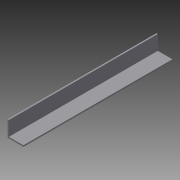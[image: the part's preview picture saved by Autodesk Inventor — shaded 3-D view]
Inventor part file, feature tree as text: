
AUTODESK INVENTOR PART (.ipt)
format: ipt  version: 2015 (Build 190159000, 159)  size: 77,824 bytes
history: native  units: in
note: dims shown in document units (in); Inventor stores cm internally (conversion verified against a paired STEP export)
features: extrude x2, sketch x2
ambient origin geometry x8: Origin, YZ Plane, XZ Plane, XY Plane, X Axis, Y Axis, Z Axis, Center Point
bodies: Solid1 (feature_tree)
feature tree (4):
  extrude  "Extrusion1"  Depth=0.125in
  extrude  "Extrusion2"  Depth=0.125in
  sketch  "Sketch1"  dims[d0=1.5in d1=0.125in]
  sketch  "Sketch2"  dims[d2=14.0in d3=0.0in d4=0.125in d5=1.5in d6=14.0in d7=0.0in]
